# Revit family: Table-Height_Adjustable-Teknion-BH_EP_Height_Adjustable_Extended_Tapered_Peninsula_Bevel_Post_Leg_Mid_Height-R2018
name_source: partatom
category: Furniture
revit_build: Autodesk Revit 2018 (Build: 20190510_1515(x64)
units: mm (PartAtom-declared; Revit-internal decimal feet)

## family parameters
Always vertical = Yes
Cut with Voids When Loaded = No
OmniClass Number = 23.40.20.00
OmniClass Title = General Furniture and Specialties
Room Calculation Point = No
Shared = Yes
Work Plane-Based = No

## types (3) — shared parameters
Arc Radius 1 = 2.875 "
Arc Radius 2 = 6 "
Assembly Code = E2020200
Manufacturer = Teknion
Manufacturer Fax = 416.661.4586
Part Number = BH_EP
Product Documentation Link = https://www.teknion.com
Product Documentation Link #2 = https://www.teknion.com
Product Documentation Link #3 = https://www.teknion.com
Product Documentation Link #4 = https://www.teknion.com
Product Line = Expansion Casegoods
Product Page URL = https://www.teknion.com
Series = Expansion Casegoods
Sustainability Data = https://www.teknion.com
URL = www.teknion.com
Unit Weight URL = http://www.teknion.com
Warranty = http://www.teknion.com

## per-type parameters (varying)
| type | Description | Model | Offset-Rectangular | Offset-Rectangular & Square |
| No Grommet | Height-Adjustable Extended Tapered Peninsula - Bevel Post Leg- Mid-Height, Mid-Height Configuration, No Grommet, Extended Range 26" to 48" | BH_EPK______N__E | No | No |
| Offset - Rectangular Grommet | Height-Adjustable Extended Tapered Peninsula - Bevel Post Leg- Mid-Height, Mid-Height Configuration, Offset - Rectangular, Extended Range 26" to 48" | BH_EPK______O__E | Yes | No |
| Offset - Retangular & Square Grommet | Height-Adjustable Extended Tapered Peninsula - Bevel Post Leg- Mid-Height, Mid-Height Configuration, Offset - Rectangular & Square, Extended Range 26" to 48" | BH_EPK______P__E | Yes | Yes |

type visibility flags (boolean, named after types; folded from table):
- No Grommet: Yes: No Grommet
- Offset - Rectangular Grommet: Yes: (none)
- Offset - Retangular & Square Grommet: Yes: (none)

## geometry (parser evidence)
native form markers: Sweep x3
no freeform markers — native parametric forms only
